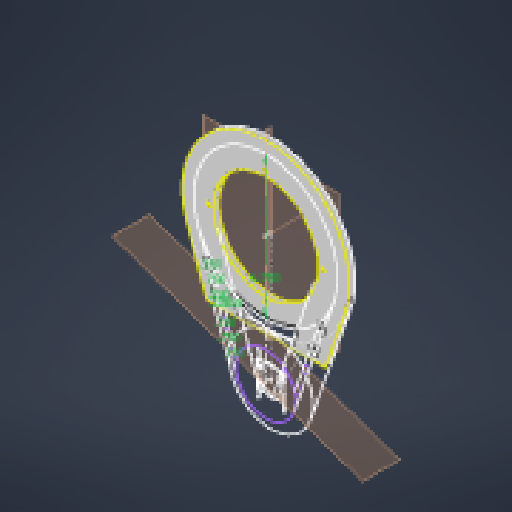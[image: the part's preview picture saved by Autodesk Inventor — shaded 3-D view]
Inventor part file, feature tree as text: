
AUTODESK INVENTOR PART (.ipt)
format: ipt  version: 2024 (Build 280153000, 153)  size: 335,360 bytes
history: native  units: in
note: dims shown in document units (in); Inventor stores cm internally (conversion verified against a paired STEP export)
features: other x7, plane x3, sketch x3, extrude x3, fillet x2, reference x2, mirror x1, hole x1, projected_geometry x1
ambient origin geometry x8: Origin, YZ Plane, XZ Plane, XY Plane, X Axis, Y Axis, Z Axis, Center Point
bodies: Solid1 (feature_tree)
feature tree (23):
  plane  "Work Plane1"
  sketch  "Sketch1"  dims[d0=0.9518in d1=6.0in]
  extrude  "Extrusion1"  Depth=6.0in
  sketch  "Sketch2"  dims[d2=0.25in d3=0.0in d4=7.874in d5=3.937in d6=1.22in]
  extrude  "Extrusion2"  Depth=3.937in
  fillet  "Fillet1"  Radius=3.937in
  fillet  "Fillet2"  Radius=1.22in
  plane  "Work Plane2"
  extrude  "Extrusion3"  Depth=0.35in
  plane  "Work Plane3"
  mirror  "Mirror1"
  hole  "Hole1"  [1 undecoded]
  reference  "Reference1"
  reference  "Reference3"
  projected_geometry  "Projected Loop1"
  sketch  "Sketch3"  dims[d7=1.22in d8=0.134in d9=0.75in d10=0.248in d11=0.25in d12=90.0deg d13=1.0in d14=0.8108in d15=0.35in d16=0.1181in d17=0.35in d18=0.1181in d19=0.35in d20=0.1181in d21=0.35in d22=0.1181in d23=0.25in d24=6.75in d26=1.0in d27=0.0in d28=0.0in d29=0.0625in d30=0.125in d32=0.25in d33=0.35in d34=0.75in d35=0.35in d36=0.35in d37=0.75in d38=0.35in d39=0.0625in d40=0.313in d41=0.0in d42=0.0in]
  other  "Work Axis1"
  other  "<userpath>\CodingProjects\C-AAM\CAD\V1\Base.iam"
  other  "Base.iam"
  other  "LazySusan:1"
  other  "OR:1"
  other  "LargePitchAssembly:1"
  other  "HTD-5-Master:1"
note: 1 required parameter value undecoded (feature->parameter linkage not recoverable at this tier; creation-order binding heuristic only, values carry confidence <= 0.55)
